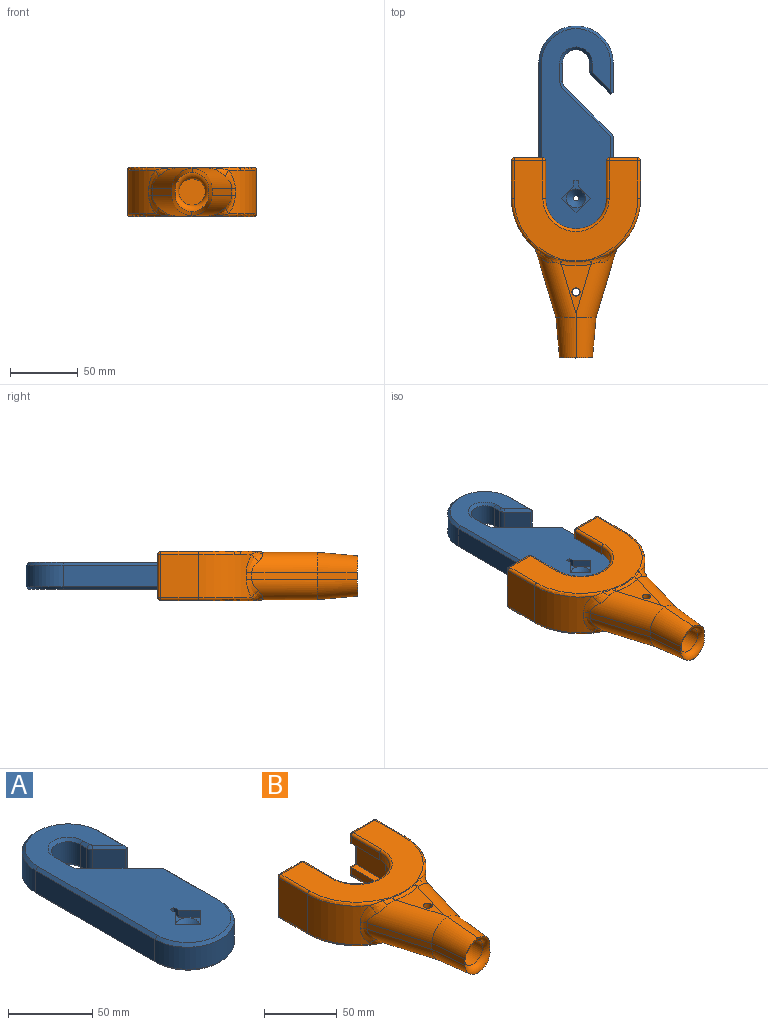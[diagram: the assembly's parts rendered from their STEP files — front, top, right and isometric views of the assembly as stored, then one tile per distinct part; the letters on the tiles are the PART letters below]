
ASSEMBLY  parts=2 mates=1
PART A: 54 faces, bbox 55x155x20 mm
  f0: cylinder r=2mm len=5mm, axis (0,0,-1), area 62.8mm2, adj f18,f53
  f1: plane 151x51mm, normal (0,0,1), area 5537.6mm2, adj f19,f20,f21,f22,f23,f24,f25,f26
  f2: plane 16x5.43mm, normal (-1,0,0), area 86.9mm2, adj f3,f14,f28,f41
  f3: cylinder r=5mm len=16mm, axis (0,0,-1), area 62.8mm2, adj f2,f4,f30,f43
  f4: plane 16x13.91mm, normal (-0.71,-0.71,0), area 314.8mm2, adj f3,f16,f31,f44
  f5: plane 22x16mm, normal (1,0,0), area 352mm2, adj f6,f16,f29,f42
  f6: cylinder r=27.5mm len=55mm, axis (0,0,-1), area 1382.3mm2, adj f5,f7,f27,f40
  f7: plane 100x16mm, normal (-1,0,0), area 1600mm2, adj f6,f8,f25,f38
  f8: cylinder r=27.5mm len=55mm, axis (0,0,-1), area 1382.3mm2, adj f7,f9,f23,f36
  f9: plane 44.64x16mm, normal (1,0,0), area 714.3mm2, adj f8,f10,f21,f34
  f10: cylinder r=5mm len=16mm, axis (0,0,-1), area 62.8mm2, adj f9,f11,f19,f32
  f11: plane 34.57x34.57mm, normal (0.71,0.71,0), area 782.3mm2, adj f10,f12,f20,f33
  f12: cylinder r=5mm len=16mm, axis (0,0,-1), area 62.8mm2, adj f11,f13,f22,f35
  f13: plane 16x13.71mm, normal (1,0,0), area 219.4mm2, adj f12,f14,f24,f37
  f14: cylinder r=10mm len=20mm, axis (0,0,-1), area 502.7mm2, adj f2,f13,f26,f39
  f15: plane 151x51mm, normal (0,0,-1), area 4182mm2, adj f17,f32,f33,f34,f35,f36,f37,f38
  f16: plane 18.12x2.12mm, normal (0.38,-0.92,0), area 39.2mm2, adj f4,f5,f29,f31,f42,f44
  f17: cylinder r=22.5mm len=45mm, axis (0,0,-1), area 706.9mm2, adj f15,f18
  f18: plane 45x45mm, normal (0,0,-1), area 1577.9mm2, adj f0,f17
  f19: cone r=3mm half-angle=45deg, axis (0,0,-1), area 8.9mm2, adj f1,f10,f20,f21
  f20: plane 35.99x35.99mm, normal (0.5,0.5,0.71), area 138.3mm2, adj f1,f11,f19,f22
  f21: plane 44.64x2mm, normal (0.71,0,0.71), area 126.3mm2, adj f1,f9,f19,f23
  f22: cone r=5mm half-angle=45deg, axis (0,0,1), area 13.3mm2, adj f1,f12,f20,f24
  f23: cone r=25.5mm half-angle=45deg, axis (0,0,-1), area 235.5mm2, adj f1,f8,f21,f25
  f24: plane 13.71x2mm, normal (0.71,0,0.71), area 38.8mm2, adj f1,f13,f22,f26
  f25: plane 100x2mm, normal (-0.71,0,0.71), area 282.8mm2, adj f1,f7,f23,f27
  f26: cone r=10mm half-angle=45deg, axis (0,0,1), area 97.7mm2, adj f1,f14,f24,f28
  f27: cone r=25.5mm half-angle=45deg, axis (0,0,-1), area 235.5mm2, adj f1,f6,f25,f29
  f28: plane 5.43x2mm, normal (-0.71,0,0.71), area 15.4mm2, adj f1,f2,f26,f30
  f29: plane 22.44x2mm, normal (0.71,0,0.71), area 61.6mm2, adj f1,f5,f16,f27,f31
  f30: cone r=3mm half-angle=45deg, axis (0,0,-1), area 8.9mm2, adj f1,f3,f28,f31
  f31: plane 15.33x14.98mm, normal (-0.5,-0.5,0.71), area 55.1mm2, adj f1,f4,f16,f29,f30
  f32: cone r=5mm half-angle=45deg, axis (0,0,1), area 8.9mm2, adj f10,f15,f33,f34
  f33: plane 35.99x35.99mm, normal (0.5,0.5,-0.71), area 138.3mm2, adj f11,f15,f32,f35
  f34: plane 44.64x2mm, normal (0.71,0,-0.71), area 126.3mm2, adj f9,f15,f32,f36
  f35: cone r=7mm half-angle=45deg, axis (0,0,-1), area 13.3mm2, adj f12,f15,f33,f37
  f36: cone r=27.5mm half-angle=45deg, axis (0,0,1), area 235.5mm2, adj f8,f15,f34,f38
  f37: plane 13.71x2mm, normal (0.71,0,-0.71), area 38.8mm2, adj f13,f15,f35,f39
  f38: plane 100x2mm, normal (-0.71,0,-0.71), area 282.8mm2, adj f7,f15,f36,f40
  f39: cone r=12mm half-angle=45deg, axis (0,0,-1), area 97.7mm2, adj f14,f15,f37,f41
  f40: cone r=27.5mm half-angle=45deg, axis (0,0,1), area 235.5mm2, adj f6,f15,f38,f42
  f41: plane 5.43x2mm, normal (-0.71,0,-0.71), area 15.4mm2, adj f2,f15,f39,f43
  f42: plane 22.44x2mm, normal (0.71,0,-0.71), area 61.6mm2, adj f5,f15,f16,f40,f44
  f43: cone r=5mm half-angle=45deg, axis (0,0,1), area 8.9mm2, adj f3,f15,f41,f44
  f44: plane 15.33x14.98mm, normal (-0.5,-0.5,-0.71), area 55.1mm2, adj f4,f15,f16,f42,f43
  f45: plane 9.11x9.11mm, normal (-0.71,-0.71,0), area 64.4mm2, adj f1,f46,f51,f52
  f46: plane 5x4mm, normal (-1,0,0), area 20mm2, adj f1,f45,f47,f52
  f47: plane 5x3mm, normal (0,-1,0), area 15mm2, adj f1,f46,f48,f52
  f48: plane 5x4mm, normal (1,0,0), area 20mm2, adj f1,f47,f49,f52
  f49: plane 9.11x9.11mm, normal (0.71,-0.71,0), area 64.4mm2, adj f1,f48,f50,f52
  f50: plane 10.61x10.61mm, normal (0.71,0.71,0), area 75mm2, adj f1,f49,f51,f52
  f51: plane 10.61x10.61mm, normal (-0.71,0.71,0), area 75mm2, adj f1,f45,f50,f52
  f52: plane 23.71x21.21mm, normal (0,0,1), area 80.8mm2, adj f45,f46,f47,f48,f49,f50,f51,f53
  f53: cone r=2mm half-angle=45deg, axis (0,0,1), area 199.9mm2, adj f0,f52
PART B: 104 faces, bbox 103.8x154.5x40.8 mm
  f0: plane 2.92x0.18mm, normal (0,-1,0), area 0.1mm2, adj f94,f95,f101
  f1: cylinder r=47.7mm len=39.3mm, axis (0,0,-1), area 1374.9mm2, adj f8,f44,f57,f72,f73,f74
  f2: plane 32.3x28mm, normal (1,0,0), area 904.4mm2, adj f9,f34,f46,f47
  f3: plane 32.3x21.2mm, normal (0,1,0), area 558.4mm2, adj f35,f36,f42,f47,f48,f54,f58,f59
  f4: plane 28x20.3mm, normal (-1,0,0), area 568.4mm2, adj f5,f10,f15,f48
  f5: cylinder r=27.7mm len=55.4mm, axis (0,0,-1), area 1766.5mm2, adj f4,f6,f10,f15
  f6: plane 28x20.3mm, normal (1,0,0), area 568.4mm2, adj f5,f10,f15,f60
  f7: plane 32.3x21.2mm, normal (0,1,0), area 558.4mm2, adj f49,f50,f55,f60,f61,f64,f67,f68
  f8: plane 32.3x28mm, normal (-1,0,0), area 904.4mm2, adj f1,f51,f61,f62
  f9: cylinder r=47.7mm len=39.3mm, axis (0,0,-1), area 1374.9mm2, adj f2,f30,f40,f89,f90,f91
  f10: plane 55.7x55.4mm, normal (0,0,-1), area 701.2mm2, adj f4,f5,f6,f11,f12,f13,f42,f55
  f11: plane 28x6mm, normal (-1,0,0), area 168mm2, adj f10,f12,f28,f36
  f12: cylinder r=22.5mm len=45mm, axis (0,0,-1), area 424.1mm2, adj f10,f11,f13,f32
  f13: plane 28x6mm, normal (1,0,0), area 168mm2, adj f10,f12,f37,f49
  f14: plane 91.4x74.22mm, normal (0,0,1), area 3540.7mm2, adj f28,f29,f30,f32,f33,f34,f35,f37
  f15: plane 55.7x55.4mm, normal (0,0,1), area 701.2mm2, adj f4,f5,f6,f16,f17,f18,f54,f64
  f16: plane 28x6mm, normal (-1,0,0), area 168mm2, adj f15,f17,f59,f66
  f17: cylinder r=22.5mm len=45mm, axis (0,0,1), area 424.1mm2, adj f15,f16,f18,f69
  f18: plane 28x6mm, normal (1,0,0), area 168mm2, adj f15,f17,f67,f71
  f19: plane 91.4x74.22mm, normal (0,0,-1), area 3540.7mm2, adj f39,f40,f45,f46,f52,f57,f58,f62
  f20: plane 48.43x14.55mm, normal (-0.96,-0.29,0), area 252.9mm2, adj f25,f27,f72,f93
  f21: plane 48.43x14.55mm, normal (0.96,-0.29,0), area 252.9mm2, adj f24,f26,f91,f96
  f22: plane 36.33x21.84mm, normal (0,0,1), area 350.8mm2, adj f26,f27,f81,f102
  f23: plane 36.33x21.84mm, normal (0,0,-1), area 350.8mm2, adj f24,f25,f82,f103
  f24: cylinder r=15mm len=56.83mm, axis (0.29,0.96,0), area 1056.3mm2, adj f21,f23,f25,f84,f86,f88,f90,f95
  f25: cylinder r=15mm len=56.83mm, axis (0.29,-0.96,0), area 1056.3mm2, adj f20,f23,f24,f74,f76,f78,f80,f94
  f26: cylinder r=15mm len=56.83mm, axis (-0.29,-0.96,0), area 1056.3mm2, adj f21,f22,f27,f83,f85,f87,f89,f97
  f27: cylinder r=15mm len=56.83mm, axis (-0.29,0.96,0), area 1056.3mm2, adj f20,f22,f26,f73,f75,f77,f79,f92
  f28: cylinder r=2mm len=28mm, axis (0,1,0), area 88mm2, adj f11,f14,f31,f32
  f29: bspline ~8.79x4.65mm, area 7.2mm2, adj f14,f30,f33,f85
  f30: torus R=45.7mm, axis (0,0,1), area 163.6mm2, adj f9,f14,f29,f34,f87
  f31: sphere r=2mm, area 10.8mm2, adj f28,f35,f36
  f32: torus R=24.5mm, axis (0,0,1), area 229.2mm2, adj f12,f14,f28,f37
  f33: torus R=46.22mm, axis (0,0,-1), area 15.9mm2, adj f14,f29,f38,f79,f81,f83
  f34: cylinder r=2mm len=28mm, axis (0,-1,0), area 88mm2, adj f2,f14,f30,f41
  f35: cylinder r=2mm len=21.2mm, axis (1,0,0), area 66.6mm2, adj f3,f14,f31,f41
  f36: cylinder r=2mm len=6mm, axis (0,0,1), area 15.7mm2, adj f3,f11,f31,f42
  f37: cylinder r=2mm len=28mm, axis (0,-1,0), area 88mm2, adj f13,f14,f32,f43
  f38: bspline ~8.44x4.59mm, area 7.2mm2, adj f14,f33,f44,f77
  f39: bspline ~8.79x4.65mm, area 7.2mm2, adj f19,f40,f45,f86
  f40: torus R=45.7mm, axis (0,0,-1), area 163.6mm2, adj f9,f19,f39,f46,f88
  f41: sphere r=2mm, area 4mm2, adj f34,f35,f47
  f42: cylinder r=2mm len=7.2mm, axis (-1,0,0), area 16.3mm2, adj f3,f10,f36,f48
  f43: sphere r=2mm, area 4mm2, adj f37,f49,f50
  f44: torus R=45.7mm, axis (0,0,1), area 163.6mm2, adj f1,f14,f38,f51,f75
  f45: torus R=46.22mm, axis (0,0,1), area 15.9mm2, adj f19,f39,f52,f80,f82,f84
  f46: cylinder r=2mm len=28mm, axis (0,-1,0), area 88mm2, adj f2,f19,f40,f53
  f47: cylinder r=2mm len=32.3mm, axis (0,0,-1), area 101.5mm2, adj f2,f3,f41,f53
  f48: cylinder r=2mm len=24.3mm, axis (0,0,-1), area 70.1mm2, adj f3,f4,f42,f54
  f49: cylinder r=2mm len=6mm, axis (0,0,1), area 15.7mm2, adj f7,f13,f43,f55
  f50: cylinder r=2mm len=21.2mm, axis (1,0,0), area 66.6mm2, adj f7,f14,f43,f56
  f51: cylinder r=2mm len=28mm, axis (0,1,0), area 88mm2, adj f8,f14,f44,f56
  f52: bspline ~8.44x4.59mm, area 7.2mm2, adj f19,f45,f57,f78
  f53: sphere r=2mm, area 4mm2, adj f46,f47,f58
  f54: cylinder r=2mm len=7.2mm, axis (-1,0,0), area 16.3mm2, adj f3,f15,f48,f59
  f55: cylinder r=2mm len=7.2mm, axis (-1,0,0), area 16.3mm2, adj f7,f10,f49,f60
  f56: sphere r=2mm, area 8.6mm2, adj f50,f51,f61
  f57: torus R=45.7mm, axis (0,0,-1), area 163.6mm2, adj f1,f19,f52,f62,f76
  f58: cylinder r=2mm len=21.2mm, axis (1,0,0), area 66.6mm2, adj f3,f19,f53,f63
  f59: cylinder r=2mm len=6mm, axis (0,0,-1), area 15.7mm2, adj f3,f16,f54,f63
  f60: cylinder r=2mm len=24.3mm, axis (0,0,-1), area 70.1mm2, adj f6,f7,f55,f64
  f61: cylinder r=2mm len=32.3mm, axis (0,0,-1), area 101.5mm2, adj f7,f8,f56,f65
  f62: cylinder r=2mm len=28mm, axis (0,1,0), area 88mm2, adj f8,f19,f57,f65
  f63: sphere r=2mm, area 8.6mm2, adj f58,f59,f66
  f64: cylinder r=2mm len=7.2mm, axis (-1,0,0), area 16.3mm2, adj f7,f15,f60,f67
  f65: sphere r=2mm, area 8.6mm2, adj f61,f62,f68
  f66: cylinder r=2mm len=28mm, axis (0,1,0), area 88mm2, adj f16,f19,f63,f69
  f67: cylinder r=2mm len=6mm, axis (0,0,-1), area 15.7mm2, adj f7,f18,f64,f70
  f68: cylinder r=2mm len=21.2mm, axis (1,0,0), area 66.6mm2, adj f7,f19,f65,f70
  f69: torus R=24.5mm, axis (0,0,-1), area 229.2mm2, adj f17,f19,f66,f71
  f70: sphere r=2mm, area 4mm2, adj f67,f68,f71
  f71: cylinder r=2mm len=28mm, axis (0,-1,0), area 88mm2, adj f18,f19,f69,f70
  f72: cylinder r=9mm len=5mm, axis (0,0,-1), area 24.5mm2, adj f1,f20,f73,f74
  f73: bspline ~17.42x9.64mm, area 79.4mm2, adj f1,f27,f72,f75
  f74: bspline ~19.31x11.1mm, area 79.4mm2, adj f1,f25,f72,f76
  f75: bspline ~12.75x9.95mm, area 56mm2, adj f27,f44,f73,f77
  f76: bspline ~12.61x9.95mm, area 56mm2, adj f25,f57,f74,f78
  f77: bspline ~8.97x5.81mm, area 22.4mm2, adj f27,f38,f75,f79
  f78: bspline ~8.97x5.81mm, area 22.4mm2, adj f25,f52,f76,f80
  f79: bspline ~4.45x4.36mm, area 3.3mm2, adj f27,f33,f77,f81
  f80: bspline ~4.45x4.36mm, area 3.3mm2, adj f25,f45,f78,f82
  f81: torus R=49.95mm, axis (0,0,1), area 66.3mm2, adj f22,f33,f79,f83
  f82: torus R=49.95mm, axis (0,0,1), area 66.3mm2, adj f23,f45,f80,f84
  f83: bspline ~4.85x4.51mm, area 3.3mm2, adj f26,f33,f81,f85
  f84: bspline ~4.85x4.51mm, area 3.3mm2, adj f24,f45,f82,f86
  f85: bspline ~8.93x5.8mm, area 22.4mm2, adj f26,f29,f83,f87
  f86: bspline ~8.93x5.8mm, area 22.4mm2, adj f24,f39,f84,f88
  f87: bspline ~12.61x9.95mm, area 56mm2, adj f26,f30,f85,f89
  f88: bspline ~12.75x9.95mm, area 56mm2, adj f24,f40,f86,f90
  f89: bspline ~19.31x11.1mm, area 79.4mm2, adj f9,f26,f87,f91
  f90: bspline ~17.42x9.64mm, area 79.4mm2, adj f9,f24,f88,f91
  f91: cylinder r=9mm len=5mm, axis (0,0,-1), area 24.5mm2, adj f9,f21,f89,f90
  f92: bspline ~36x16.69mm, area 632.3mm2, adj f27,f93,f97,f98,f101
  f93: plane 30x5.55mm, normal (-1,-0.09,0), area 147.4mm2, adj f20,f92,f94,f101
  f94: bspline ~36x16.69mm, area 632.3mm2, adj f0,f25,f93,f95,f101
  f95: bspline ~36x16.69mm, area 632.3mm2, adj f0,f24,f94,f96,f101
  f96: plane 30x5.55mm, normal (1,-0.09,0), area 147.4mm2, adj f21,f95,f97,f101
  f97: bspline ~36x16.69mm, area 632.3mm2, adj f26,f92,f96,f98,f101
  f98: plane 2.92x0.18mm, normal (0,-1,0), area 0.1mm2, adj f92,f97,f101
  f99: cylinder r=9.75mm len=65mm, axis (0,-1,0), area 3929.8mm2, adj f100,f101,f102,f103
  f100: plane 19.5x19.5mm, normal (0,-1,0), area 298.6mm2, adj f99
  f101: torus R=14.75mm, axis (0,-1,0), area 461.1mm2, adj f0,f92,f93,f94,f95,f96,f97,f98
  f102: cylinder r=3mm len=8.22mm, axis (0,0,1), area 155mm2, adj f22,f99
  f103: cylinder r=3mm len=8.22mm, axis (0,0,1), area 148.3mm2, adj f23,f99
PLACE A t=(-43.84,-0.41,-28.22)mm
PLACE B t=(-43.84,-0.41,-18.29)mm
MATE cylindrical A.f8 <-> B.f5  axis (0,0,-1) through (-43.84,-0.41,-10.22)mm
